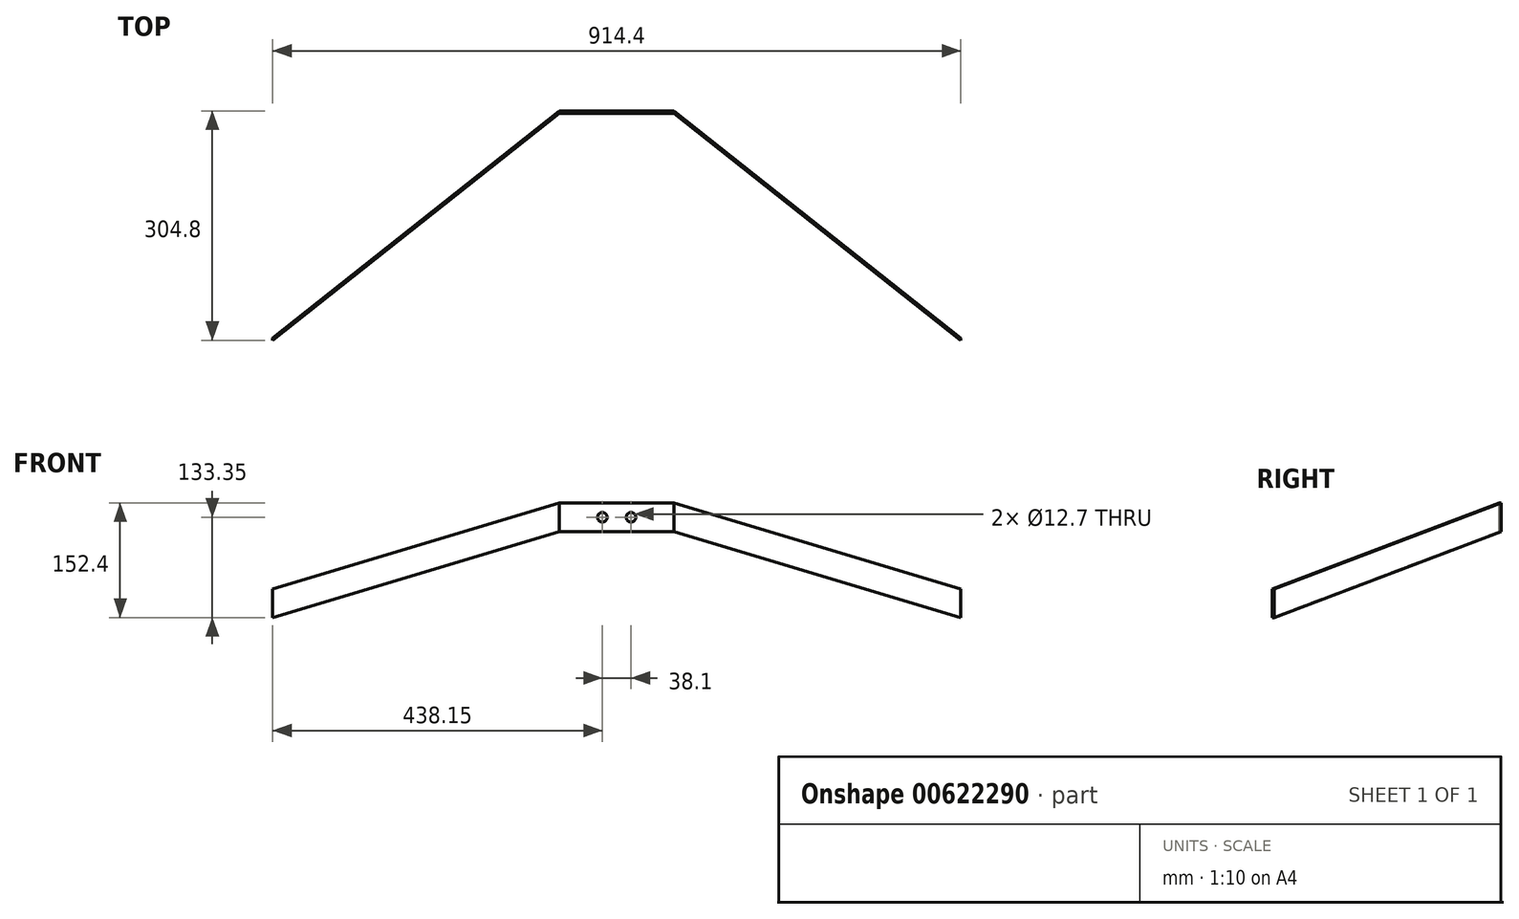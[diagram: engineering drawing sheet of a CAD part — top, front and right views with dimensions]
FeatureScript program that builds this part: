
annotation { "Feature Type Name" : "Feature", "Feature Type Description" : "" }
export const myFeature = defineFeature(function(context is Context, id is Id, definition is map)
    precondition{}
    {
        {
            var Q0;
            Q0=qCreatedBy(makeId("Front.planeOp"),FACE);
            var sketch = newSketch(context, id + "F0", { "sketchPlane" : qUnion([Q0])});
            skLineSegment(sketch, "E0.bottom", {"start": v(0, 0) * mm, "end": v(-914.4, 0) * mm});
            skLineSegment(sketch, "E0.top", {"start": v(0, -152.4) * mm, "end": v(-914.4, -152.4) * mm});
            skLineSegment(sketch, "E0.left", {"start": v(0, 0) * mm, "end": v(0, -152.4) * mm});
            skLineSegment(sketch, "E0.right", {"start": v(-914.4, 0) * mm, "end": v(-914.4, -152.4) * mm});
            skSolve(sketch);
        }
        {
            var Q0;
            Q0 = qSketchRegion(id + "F0", true);
            extrude(context, id + "F1", {"entities" : qUnion([Q0]), "depth" : 304.8 * mm, "offsetDistance" : 25.4 * mm});
        }
        {
            var Q0;
            Q0=makeQuery(id+"F1.opExtrude","SWEPT_FACE",FACE,{"disambiguationData":[OSD([sQuery(id+"F0.wireOp",EDGE,"E0.bottom")])]});
            var sketch = newSketch(context, id + "F2", { "sketchPlane" : qUnion([Q0])});
            skLineSegment(sketch, "E1", {"start": v(-457.2, 0) * mm, "end": v(-457.2, -304.8) * mm, "construction": true});
            skLineSegment(sketch, "E2.top", {"start": v(-533.4, -3.18) * mm, "end": v(-381, -3.17) * mm});
            skLineSegment(sketch, "E3", {"start": v(-914.4, -304.8) * mm, "end": v(-533.4, -3.18) * mm});
            skLineSegment(sketch, "E4", {"start": v(-381, -3.18) * mm, "end": v(0, -304.8) * mm});
            skLineSegment(sketch, "E5", {"start": v(0, -304.8) * mm, "end": v(-914.4, -304.8) * mm});
            skSolve(sketch);
        }
        {
            var Q0;
            Q0 = qSketchRegion(id + "F2", true);
            extrude(context, id + "F3", {"entities" : qUnion([Q0]), "operationType" : NewBodyOperationType.REMOVE, "endBound" : BoundingType.THROUGH_ALL, "oppositeDirection" : true, "depth" : 25.4 * mm, "offsetDistance" : 25.4 * mm});
        }
        {
            var Q0;
            Q0=makeQuery(id+"F1.opExtrude","SWEPT_FACE",FACE,{"disambiguationData":[OSD([sQuery(id+"F0.wireOp",EDGE,"E0.bottom")])]});
            var sketch = newSketch(context, id + "F4", { "sketchPlane" : qUnion([Q0])});
            skLineSegment(sketch, "E6", {"start": v(-533.4, -3.18) * mm, "end": v(-533.4, 0) * mm, "construction": true});
            skPoint(sketch, "E7", {"position": v(-914.4, -301.63) * mm});
            skLineSegment(sketch, "E8", {"start": v(-914.4, -301.63) * mm, "end": v(-533.4, 0) * mm});
            skLineSegment(sketch, "E9", {"start": v(-533.4, 0) * mm, "end": v(-914.4, 0) * mm});
            skLineSegment(sketch, "E10", {"start": v(-914.4, 0) * mm, "end": v(-914.4, -301.63) * mm});
            skSolve(sketch);
        }
        {
            var Q0;
            Q0 = qSketchRegion(id + "F4", true);
            extrude(context, id + "F5", {"entities" : qUnion([Q0]), "operationType" : NewBodyOperationType.REMOVE, "endBound" : BoundingType.THROUGH_ALL, "oppositeDirection" : true, "depth" : 25.4 * mm, "offsetDistance" : 25.4 * mm});
        }
        {
            var Q0;
            Q0=makeQuery(id+"F1.opExtrude","SWEPT_FACE",FACE,{"disambiguationData":[OSD([sQuery(id+"F0.wireOp",EDGE,"E0.bottom")])]});
            var sketch = newSketch(context, id + "F6", { "sketchPlane" : qUnion([Q0])});
            skLineSegment(sketch, "E11", {"start": v(-381, -3.17) * mm, "end": v(-381, 0) * mm, "construction": true});
            skPoint(sketch, "E12", {"position": v(0, -301.63) * mm});
            skLineSegment(sketch, "E13", {"start": v(-381, 0) * mm, "end": v(0, -301.63) * mm});
            skLineSegment(sketch, "E14", {"start": v(0, -301.63) * mm, "end": v(0, 0) * mm});
            skLineSegment(sketch, "E15", {"start": v(0, 0) * mm, "end": v(-381, 0) * mm});
            skSolve(sketch);
        }
        {
            var Q0;
            Q0 = qSketchRegion(id + "F6", true);
            extrude(context, id + "F7", {"entities" : qUnion([Q0]), "operationType" : NewBodyOperationType.REMOVE, "endBound" : BoundingType.THROUGH_ALL, "oppositeDirection" : true, "depth" : 25.4 * mm, "offsetDistance" : 25.4 * mm});
        }
        {
            var Q0;
            Q0=makeQuery(id+"F1.opExtrude","CAP_FACE",FACE,{"disambiguationData":[OSD([sQuery(id+"F0.wireOp",EDGE,"E0.bottom"),sQuery(id+"F0.wireOp",EDGE,"E0.top"),sQuery(id+"F0.wireOp",EDGE,"E0.left"),sQuery(id+"F0.wireOp",EDGE,"E0.right")])],"isStart":true});
            var sketch = newSketch(context, id + "F8", { "sketchPlane" : qUnion([Q0])});
            skPoint(sketch, "E16", {"position": v(381, -38.1) * mm});
            skPoint(sketch, "E17", {"position": v(533.4, -38.1) * mm});
            skLineSegment(sketch, "E18", {"start": v(0, -152.4) * mm, "end": v(381, -38.1) * mm});
            skLineSegment(sketch, "E19", {"start": v(914.4, -152.4) * mm, "end": v(0, -152.4) * mm});
            skLineSegment(sketch, "E20", {"start": v(914.4, -152.4) * mm, "end": v(533.4, -38.1) * mm});
            skLineSegment(sketch, "E21", {"start": v(381, -38.1) * mm, "end": v(533.4, -38.1) * mm});
            skSolve(sketch);
        }
        {
            var Q0;
            Q0 = qSketchRegion(id + "F8", true);
            extrude(context, id + "F9", {"entities" : qUnion([Q0]), "operationType" : NewBodyOperationType.REMOVE, "endBound" : BoundingType.THROUGH_ALL, "oppositeDirection" : true, "depth" : 25.4 * mm, "offsetDistance" : 25.4 * mm});
        }
        {
            var Q0;
            Q0=makeQuery(id+"F1.opExtrude","CAP_FACE",FACE,{"disambiguationData":[OSD([sQuery(id+"F0.wireOp",EDGE,"E0.bottom"),sQuery(id+"F0.wireOp",EDGE,"E0.top"),sQuery(id+"F0.wireOp",EDGE,"E0.left"),sQuery(id+"F0.wireOp",EDGE,"E0.right")])],"isStart":true});
            var sketch = newSketch(context, id + "F10", { "sketchPlane" : qUnion([Q0])});
            skLineSegment(sketch, "E22", {"start": v(381, 0) * mm, "end": v(0, -114.3) * mm});
            skLineSegment(sketch, "E23", {"start": v(0, -114.3) * mm, "end": v(0, 0) * mm});
            skLineSegment(sketch, "E24", {"start": v(0, 0) * mm, "end": v(381, 0) * mm});
            skSolve(sketch);
        }
        {
            var Q0;
            Q0 = qSketchRegion(id + "F10", true);
            extrude(context, id + "F11", {"entities" : qUnion([Q0]), "operationType" : NewBodyOperationType.REMOVE, "endBound" : BoundingType.THROUGH_ALL, "oppositeDirection" : true, "depth" : 25.4 * mm, "offsetDistance" : 25.4 * mm});
        }
        {
            var Q0;
            Q0=makeQuery(id+"F1.opExtrude","CAP_FACE",FACE,{"disambiguationData":[OSD([sQuery(id+"F0.wireOp",EDGE,"E0.bottom"),sQuery(id+"F0.wireOp",EDGE,"E0.top"),sQuery(id+"F0.wireOp",EDGE,"E0.left"),sQuery(id+"F0.wireOp",EDGE,"E0.right")])],"isStart":true});
            var sketch = newSketch(context, id + "F12", { "sketchPlane" : qUnion([Q0])});
            skLineSegment(sketch, "E25", {"start": v(533.4, 0) * mm, "end": v(914.4, -114.3) * mm});
            skLineSegment(sketch, "E26", {"start": v(914.4, -114.3) * mm, "end": v(914.4, 0) * mm});
            skLineSegment(sketch, "E27", {"start": v(914.4, 0) * mm, "end": v(533.4, 0) * mm});
            skSolve(sketch);
        }
        {
            var Q0;
            Q0 = qSketchRegion(id + "F12", true);
            extrude(context, id + "F13", {"entities" : qUnion([Q0]), "operationType" : NewBodyOperationType.REMOVE, "endBound" : BoundingType.THROUGH_ALL, "oppositeDirection" : true, "depth" : 25.4 * mm, "offsetDistance" : 25.4 * mm});
        }
        {
            var Q0;
            Q0=makeQuery(id+"F3.boolean.opBoolean","COPY",FACE,{"derivedFrom":makeQuery(id+"F3.opExtrude","SWEPT_FACE",FACE,{"disambiguationData":[OSD([sQuery(id+"F2.wireOp",EDGE,"E2.top")])]})});
            var sketch = newSketch(context, id + "F14", { "sketchPlane" : qUnion([Q0])});
            skPoint(sketch, "E28", {"position": v(-476.25, -19.05) * mm});
            skPoint(sketch, "E29", {"position": v(-438.15, -19.05) * mm});
            skLineSegment(sketch, "E30", {"start": v(-457.2, 0) * mm, "end": v(-457.2, -38.1) * mm, "construction": true});
            skSolve(sketch);
        }
        {
            var Q0;
            Q0=sQuery(id+"F14.wireOp",VERTEX,"E28");
            var Q1;
            Q1=sQuery(id+"F14.wireOp",VERTEX,"E29");
            var Q2;
            Q2=makeQuery(id+"F1.opExtrude","SWEPT_BODY",BODY,{"disambiguationData":[OSD([sQuery(id+"F0.wireOp",EDGE,"E0.bottom"),sQuery(id+"F0.wireOp",EDGE,"E0.top"),sQuery(id+"F0.wireOp",EDGE,"E0.left"),sQuery(id+"F0.wireOp",EDGE,"E0.right")])]});
            hole(context, id + "F15", {"style" : HoleStyle.SIMPLE, "endStyle" : HoleEndStyle.THROUGH, "holeDiameter" : 12.7 * mm, "majorDiameter" : 6.35 * mm, "isTappedThrough" : true, "tappedDepth" : 12.7 * mm, "tapClearance" : 3, "startFromSketch" : true, "locations" : qUnion([Q0, Q1]), "scope" : qUnion([Q2])});
        }
    });
